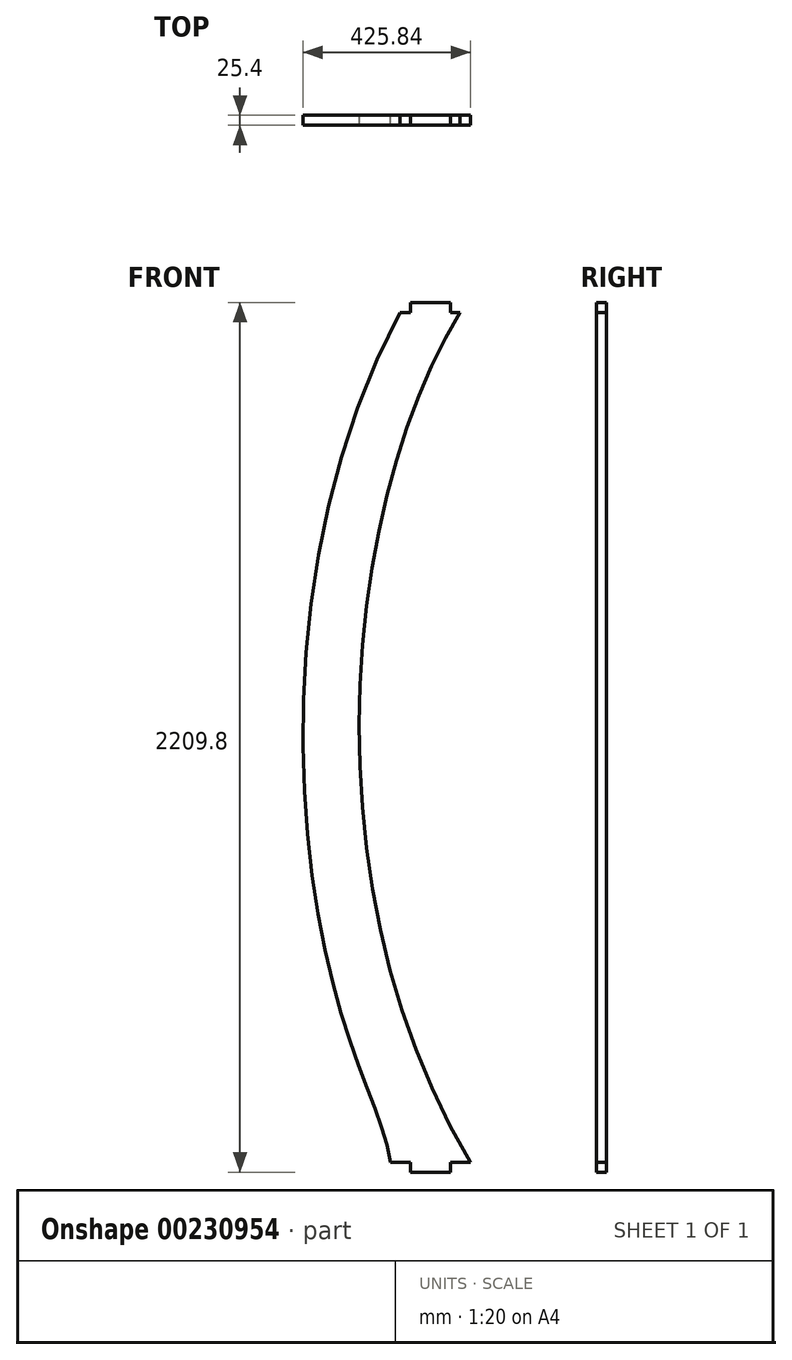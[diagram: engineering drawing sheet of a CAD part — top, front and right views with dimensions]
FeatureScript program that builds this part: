
annotation { "Feature Type Name" : "Feature", "Feature Type Description" : "" }
export const myFeature = defineFeature(function(context is Context, id is Id, definition is map)
    precondition{}
    {
        {
            var Q0;
            Q0=qCreatedBy(makeId("Front.planeOp"),FACE);
            var sketch = newSketch(context, id + "F0", { "sketchPlane" : qUnion([Q0])});
            skLineSegment(sketch, "E0", {"start": v(0, -1193.8) * mm, "end": v(-919.23, -1193.8) * mm});
            skLineSegment(sketch, "E1", {"start": v(0, 965.2) * mm, "end": v(-945.58, 965.2) * mm});
            skFitSpline(sketch, "E2", {"points": [v(-945.58, 965.2) * mm, v(-919.23, -1193.8) * mm], "startDerivative": vector(-889.45, -1441.33) * mm, "endDerivative": vector(1263.87, -2098.17) * mm});
            skLineSegment(sketch, "E3", {"start": v(-945.58, 965.2) * mm, "end": v(-1097.98, 965.2) * mm});
            skLineSegment(sketch, "E4", {"start": v(-919.23, -1193.8) * mm, "end": v(-1122.43, -1193.8) * mm});
            skFitSpline(sketch, "E5", {"points": [v(-1097.98, 965.2) * mm, v(-1266.7, -749.28) * mm, v(-1122.43, -1193.8) * mm], "startDerivative": vector(-1456.54, -2733.7) * mm, "endDerivative": vector(159.23, -982.95) * mm});
            skSolve(sketch);
        }
        {
            var Q0;
            Q0=qSketchRegion(id+"F0",true);
            extrude(context, id + "F1", {"entities" : qUnion([Q0]), "endBound" : BoundingType.SYMMETRIC, "depth" : 25.4 * mm});
        }
        {
            var Q0;
            Q0=makeQuery(id+"F1.opExtrude","CAP_FACE",FACE,{"disambiguationData":[OSD([sQuery(id+"F0.wireOp",EDGE,"E2"),sQuery(id+"F0.wireOp",EDGE,"E3"),sQuery(id+"F0.wireOp",EDGE,"E4"),sQuery(id+"F0.wireOp",EDGE,"E5")])],"isStart":false});
            var sketch = newSketch(context, id + "F2", { "sketchPlane" : qUnion([Q0])});
            skLineSegment(sketch, "E6.bottom", {"start": v(-1071.63, -1193.8) * mm, "end": v(-970.03, -1193.8) * mm});
            skLineSegment(sketch, "E6.top", {"start": v(-1071.63, -1219.2) * mm, "end": v(-970.03, -1219.2) * mm});
            skLineSegment(sketch, "E6.left", {"start": v(-1071.63, -1193.8) * mm, "end": v(-1071.63, -1219.2) * mm});
            skLineSegment(sketch, "E6.right", {"start": v(-970.03, -1193.8) * mm, "end": v(-970.03, -1219.2) * mm});
            skPoint(sketch, "E6.middle", {"position": v(-1020.83, -1206.5) * mm});
            skPoint(sketch, "E6.middle.positionSnap0", {"position": v(-1020.83, -1193.8) * mm});
            skPoint(sketch, "E6.centerSnap0", {"position": v(-1020.83, -1193.8) * mm});
            skLineSegment(sketch, "E7.bottom", {"start": v(-1071.63, 965.2) * mm, "end": v(-970.03, 965.2) * mm});
            skLineSegment(sketch, "E7.top", {"start": v(-1071.63, 990.6) * mm, "end": v(-970.03, 990.6) * mm});
            skLineSegment(sketch, "E7.left", {"start": v(-1071.63, 965.2) * mm, "end": v(-1071.63, 990.6) * mm});
            skLineSegment(sketch, "E7.right", {"start": v(-970.03, 965.2) * mm, "end": v(-970.03, 990.6) * mm});
            skPoint(sketch, "E7.middle", {"position": v(-1020.83, 977.9) * mm});
            skSolve(sketch);
        }
        {
            var Q0;
            Q0=makeQuery(id+"F2.imprint","IMPRINT",FACE,{"disambiguationData":[TD([[makeQuery(id+"F2.imprint","IMPRINT",EDGE,{"derivedFrom":sQuery(id+"F2.wireOp",EDGE,"E7.bottom")}),-1.0]])]});
            var Q1;
            Q1=makeQuery(id+"F2.imprint","IMPRINT",FACE,{"disambiguationData":[TD([[makeQuery(id+"F2.imprint","IMPRINT",EDGE,{"derivedFrom":sQuery(id+"F2.wireOp",EDGE,"E6.bottom")}),1.0]])]});
            var Q2;
            Q2=makeQuery(id+"F1.opExtrude","CAP_FACE",FACE,{"disambiguationData":[OSD([sQuery(id+"F0.wireOp",EDGE,"E2"),sQuery(id+"F0.wireOp",EDGE,"E3"),sQuery(id+"F0.wireOp",EDGE,"E4"),sQuery(id+"F0.wireOp",EDGE,"E5")])],"isStart":true});
            extrude(context, id + "F3", {"entities" : qUnion([Q0, Q1]), "operationType" : NewBodyOperationType.ADD, "endBound" : BoundingType.UP_TO_SURFACE, "oppositeDirection" : true, "endBoundEntityFace" : qUnion([Q2]), "depth" : 25.4 * mm});
        }
    });
